# Revit family: AC-S4T - Yoke Mount
name_source: partatom
category: Generic Models
revit_build: Autodesk Revit 2014 (Build: 20130308_1515(x64)
units: mm (PartAtom-declared; Revit-internal decimal feet)

## types (1)
- AC-S4T - Yoke Mount
    100V Taps = 16, 8, 4, 2
    70V Taps = 16, 8, 4, 2, 1
    Coverage Horizontal = 130.00°
    Coverage Vertical = 130.00°
    Default Elevation = 8' - 0"
    Depth = 0' - 11 23/32"
    Description = 4" 2-Way Surface Mount Loudspeaker
    Height = 1' - 11 15/32"
    Impedance = 8
    Manufacturer = QSC Audio Products, LLC
    Manufacturer URL = www.qsc.com
    Model = AC-S4T
    Mount Depth = 0' - 10"
    Mount Height = 1' - 11 17/32"
    Mount Width = 0' - 4 17/32"
    Power Handling = 16
    Product Documentation Link = TBA
    Product Page URL = TBA
    Regulatory Compliance = RoHS
    SPL Max = 103
    Sensitivity = 85
    URL = TBA
    Weight Dimensional (kg) = 5.3
    Weight Dimensional (lb) = 11.8
    Weight Product (kg) = 2.4
    Weight Product (lb) = 5.3
    Width = 0' - 6 5/16"

## geometry (parser evidence)
native form markers: Blend x1, Sweep x4
no freeform markers — native parametric forms only
